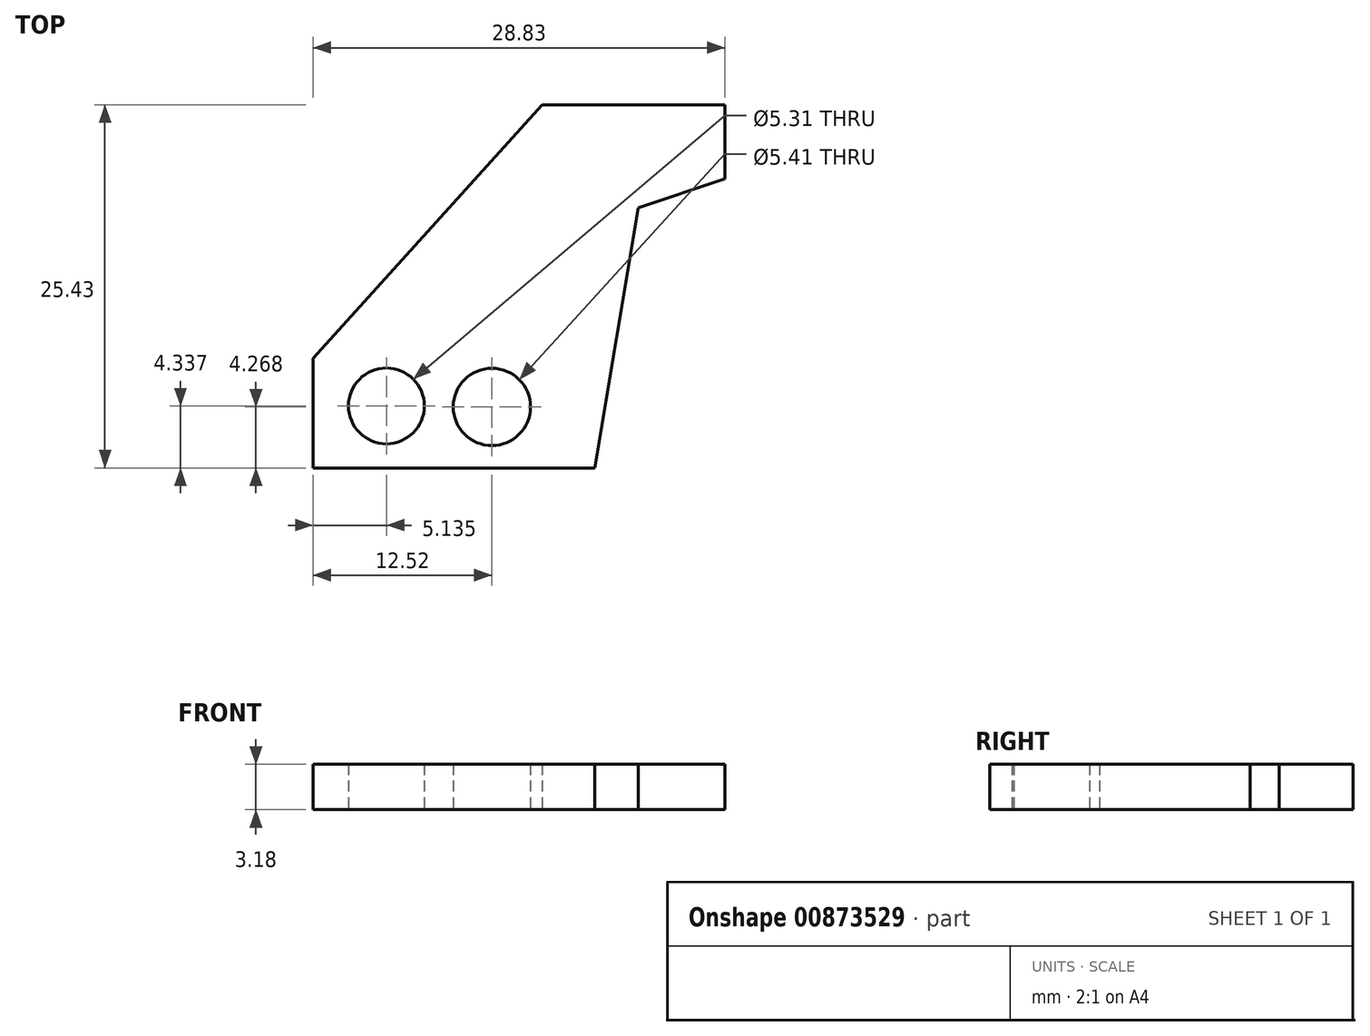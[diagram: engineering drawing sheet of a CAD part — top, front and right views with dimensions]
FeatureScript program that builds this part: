
annotation { "Feature Type Name" : "Feature", "Feature Type Description" : "" }
export const myFeature = defineFeature(function(context is Context, id is Id, definition is map)
    precondition{}
    {
        {
            var Q0;
            Q0=qCreatedBy(makeId("Top.planeOp"),FACE);
            var sketch = newSketch(context, id + "F0", { "sketchPlane" : qUnion([Q0])});
            skLineSegment(sketch, "E0", {"start": v(0, 0) * mm, "end": v(0, 7.66) * mm});
            skLineSegment(sketch, "E1", {"start": v(0, 7.66) * mm, "end": v(16.02, 25.43) * mm});
            skLineSegment(sketch, "E2", {"start": v(16.02, 25.43) * mm, "end": v(28.83, 25.43) * mm});
            skLineSegment(sketch, "E3", {"start": v(28.83, 25.43) * mm, "end": v(28.83, 20.25) * mm});
            skLineSegment(sketch, "E4", {"start": v(28.83, 20.25) * mm, "end": v(22.77, 18.2) * mm});
            skLineSegment(sketch, "E5", {"start": v(22.77, 18.2) * mm, "end": v(19.7, 0) * mm});
            skLineSegment(sketch, "E6", {"start": v(19.7, 0) * mm, "end": v(0, 0) * mm});
            skCircle(sketch, "E7", {"center": v(5.13, 4.34) * mm, "radius": 2.65 * mm});
            skPoint(sketch, "E7.first.point", {"position": v(3.51, 2.24) * mm});
            skPoint(sketch, "E7.second.point", {"position": v(3.26, 6.22) * mm});
            skPoint(sketch, "E7.third.point", {"position": v(7.74, 4.85) * mm});
            skCircle(sketch, "E8", {"center": v(12.52, 4.27) * mm, "radius": 2.7 * mm});
            skPoint(sketch, "E8.first.point", {"position": v(9.82, 4.46) * mm});
            skPoint(sketch, "E8.second.point", {"position": v(12.76, 6.96) * mm});
            skPoint(sketch, "E8.third.point", {"position": v(14.6, 2.55) * mm});
            skSolve(sketch);
        }
        {
            var Q0;
            Q0 = qSketchRegion(id + "F0", true);
            var Q1;
            Q1=makeQuery(id+"FmYxqtNAYWRYq0s.importOp","IMPORT",FACE,{"importTag":48.0});
            extrude(context, id + "F1", {"entities" : qUnion([Q0]), "depth" : 3.17 * mm, "endBoundEntityFace" : qUnion([Q1]), "offsetDistance" : 25.4 * mm});
        }
    });
